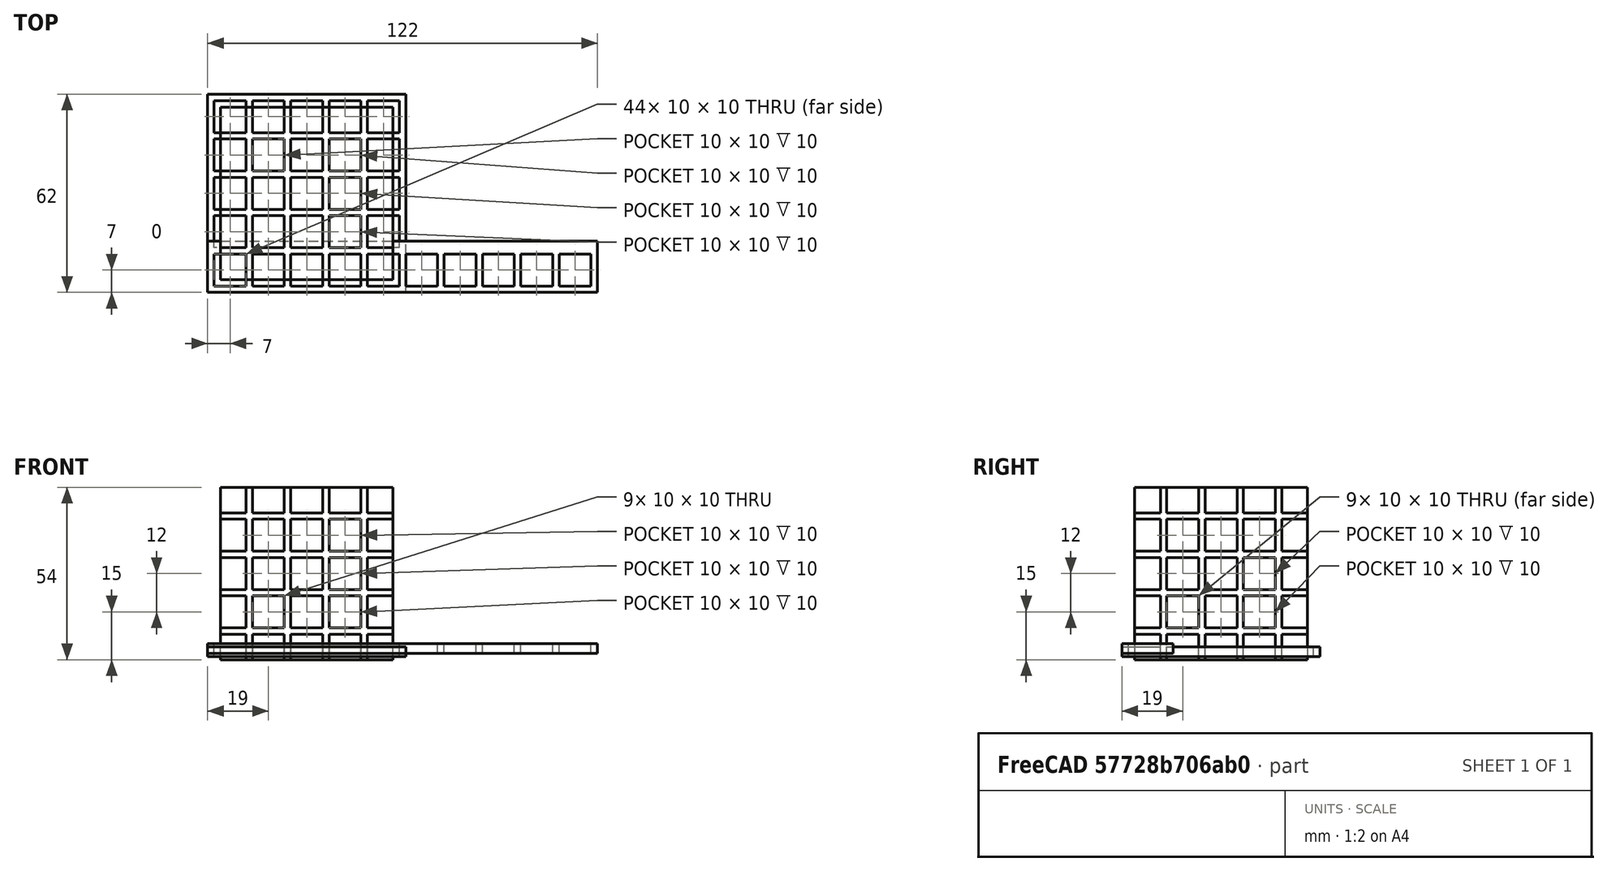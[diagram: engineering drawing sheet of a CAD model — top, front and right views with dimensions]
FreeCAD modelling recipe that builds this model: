
FCSTD DOCUMENT  (FreeCAD 0.18.4R)
Label: tutorial_freecad_ex10_a
License: All rights reserved
LicenseURL: http://en.wikipedia.org/wiki/All_rights_reserved
objects: Part::Box×4, Part::FeaturePython×3, Part::Cut×3
note: 10 computed .brp shape members not serialized (recipe doc carries the construction recipe); baked Part::Feature solids carry a one-line shape summary decoded from their .brp

FEATURE [Part::Box] Box  label="master_box"
  AttacherType = Attacher::AttachEngine3D
  Height = 10
  Length = 10
  Width = 10
FEATURE [Part::FeaturePython] Array  # Draft array (typed FeaturePython)
  Angle = 360
  ArrayType = 0
  Axis = (0,0,1)
  Base = -> Box
  Center = (0,0,0)
  Fuse = false
  IntervalAxis = (0,0,0)
  IntervalX = (12,0,0)
  IntervalY = (0,1,0)
  IntervalZ = (0,0,1)
  NumberPolar = 1
  NumberX = 10
  NumberY = 1
  NumberZ = 1
FEATURE [Part::Box] Box001  label="Cubo"
  AttacherType = Attacher::AttachEngine3D
  Height = 3
  Length = 122
  Placement = pos=(-2,-2,4) rot=(0,0,1;0rad)
  Width = 16
FEATURE [Part::Cut] Cut
  Base = -> Box001
  Refine = true
  Tool = -> Array
FEATURE [Part::FeaturePython] Array001  # Draft array (typed FeaturePython)
  Angle = 360
  ArrayType = 0
  Axis = (0,0,1)
  Base = -> Box
  Center = (0,0,0)
  Fuse = false
  IntervalAxis = (0,0,0)
  IntervalX = (12,0,0)
  IntervalY = (0,12,0)
  IntervalZ = (0,0,1)
  NumberPolar = 1
  NumberX = 5
  NumberY = 5
  NumberZ = 1
FEATURE [Part::Box] Box002  label="Cubo001"
  AttacherType = Attacher::AttachEngine3D
  Height = 3
  Length = 62
  Placement = pos=(-2,-2,3) rot=(0,0,1;0rad)
  Width = 62
FEATURE [Part::Cut] Cut001
  Base = -> Box002
  Refine = true
  Tool = -> Array001
FEATURE [Part::FeaturePython] Array002  # Draft array (typed FeaturePython)
  Angle = 360
  ArrayType = 0
  Axis = (0,0,1)
  Base = -> Box
  Center = (0,0,0)
  Fuse = false
  IntervalAxis = (0,0,0)
  IntervalX = (12,0,0)
  IntervalY = (0,12,0)
  IntervalZ = (0,0,12)
  NumberPolar = 1
  NumberX = 5
  NumberY = 5
  NumberZ = 5
FEATURE [Part::Box] Box003  label="Cubo002"
  AttacherType = Attacher::AttachEngine3D
  Height = 54
  Length = 54
  Placement = pos=(2,2,2) rot=(0,0,1;0rad)
  Width = 54
FEATURE [Part::Cut] Cut002
  Base = -> Box003
  Refine = true
  Tool = -> Array002
